# Revit family: VS F Global Expuesto
name_source: partatom
category: Plumbing Fixtures
revit_build: Autodesk Revit 2015 (Build: 20140322_1515(x64)
units: mm (PartAtom-declared; Revit-internal decimal feet)

## types (1)
- VS F Global Expuesto
    Assembly Code = D2010.60
    BT_Color = Blanco
    BT_Itemizado_Estandar_CDT = E 04 02 00
    BT_Material = Loza
    BT_SKU = 00 00 00
    BT_Uso = Baño
    Depth = 553 mm
    Description = Vaso discapacitados para fluxor EXPUESTO
Modelo: GLOBAL
Instalación: Desplazado del muro 140 mm (distancia mínima)
Descarga Piso:
Con manguito 25= 290 mm del eje a muro terminado
Con manguito 21= 240mm del eje a muro terminado
Altura: 472 mm (sin asiento)
Fijación piso: Incluida
SKU : WCS-31-0071
    Height = 472 mm
    ID_Objeto = BT_F_F_1793
    ID_Source = BIMTOOL
    Keynote = 22 41 13.13
    Manufacturer = Klipen
    Model = VS F Global Expuesto
    Supplier = Mk
    Type Comments = Vaso discapacitados para fluxor EXPUESTO
Modelo: GLOBAL
Instalación: Desplazado del muro 140 mm (distancia mínima)
Descarga Piso:
Con manguito 25= 290 mm del eje a muro terminado
Con manguito 21= 240mm del eje a muro terminado
Altura: 472 mm (sin asiento)
Fijación piso: Incluida
SKU : WCS-31-0071
    URL = www.mk.cl
    Width = 375 mm

## geometry (parser evidence)
native form markers: Blend x6, Extrusion x2, Sweep x4
no freeform markers — native parametric forms only
